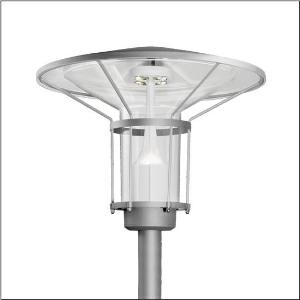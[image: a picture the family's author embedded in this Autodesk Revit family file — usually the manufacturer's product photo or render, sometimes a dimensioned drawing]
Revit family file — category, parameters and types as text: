
# Revit family: laterne_classic_iq___pl1_2s_5xa5245of14h_0553
name_source: partatom
category: Lighting Fixtures
units: mm (PartAtom-declared; Revit-internal decimal feet)

## family parameters
Cut with Voids When Loaded = No
Host = Face
Light Source = No
Part Type = Normal
Room Calculation Point = No
Round Connector Dimension = Use Diameter
Shared = No

## types (1)
- --- (1 x LED, 2670 lm, 21.8 W, 2700K)
    Apparent Load = 22 VA
    CIE Flux Codes = 21 60 93 97 100
    Color Rendering = 70
    Color Temperature = 2700K
    Default Elevation = 1800 mm
    Description = Lantern Classic iQ, mast luminaire, Module 540 iQ-SR, primary light control with 3 zone facetted reflector, of plastic, silver coated, highly specular, structured, primary optical cover: cover, of PMMA, transparent, light distribution: PL1.2s, light emission: direct distribution, primary light characteristic: symmetric, installation type: post-top, LED, High Power LED, rated luminous flux: 2.970lm, luminous efficacy: 136lm/W, light colour: 727, colour temperature: 2700K, control gear: ECG iQ, control: presetting dimming logarithmic, Street-Remote, Auto-Match, Temp-Guard, Lumen-Switch, Night-Set, Smart-Wire, Light-Fading, Desk-Remote (wireless, voltage-free reading and setting of iQ features in the workshop via application-optimized NFC function/RFID function), optimised constant luminous flux control (CLO 2.0), with terminal, 6-pole, max. 2.5mm², mains connection: 230..240V, AC, 50/60Hz, start of lifetime: 22W, end of service life: 23W, reduction: 11W, luminaire housing, upper part, of glass-fibre reinforced polyester, coated, Siteco® metallic grey (DB 702S), diameter: 750mm, height: 596mm, spigot size: d x l = 76 x 70mm (post-top) | with reducer (optional accessory) 60 x 70mm, post-top mast mounting element, of diecast aluminium, coated, Siteco® metallic grey (DB 702S), Module 540 iQ-SR, traffic white (RAL 9016), equipment: standard, protection rating (complete): IP65, insulation class (complete): insulation class II (safety insulation), certification: CE, ENEC, VDE, packaging unit: 1 piece

Light Distribution: PL1.2s
    Height = 596 mm
    Lamp = 1 x LED
    Lamp Light Flux = 2670 lm
    Lamp Power = 21.8 W
    Lamp count = 1
    Length = 750 mm
    Luminous efficacy = 122 lm/W
    Manufacturer = Siteco
    ModVariant = No
    Model = 5XA5245OF14H
    Number of Poles = 1
    OnlyDefault = Yes
    Power Factor = 1
    Product Name = Laterne Classic iQ | PL1.2s
    Product group = mast luminaire | pylon top
    ProductGroupID = 6100
    Protection Class = Protection class II
    Protection Degree = IP 65
    RLX_Detail_Level = 1
    RLX_Emergency_Light_Flux = 0 lm
    RLX_Emergency_Type = 0
    RLX_Emergency_Type_DB = No
    RlxData = <blob elided: 62585 chars, md5=c4146125>
    Socket = socket
    Standby Power = 0 W
    System Light Flux = 2670 lm
    System Power = 22 W
    Type Comments = factory setting: luminous flux: 100 % | dim-lin: 254 | 456 mA
    Type Image = l_1006052.jpg
    URL = http://relux.com
    VarID = @adj_095199
    Voltage = 0 V
    Weight = 0.00 kg
    Width = 0 mm  [stored 0 ft]

note: [stored X ft] marks values corroborated as IEEE doubles in the binary element streams (Revit-internal decimal feet)

## geometry (parser evidence)
native form markers: Blend x4, Sweep x9
no freeform markers — native parametric forms only
